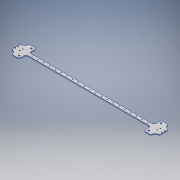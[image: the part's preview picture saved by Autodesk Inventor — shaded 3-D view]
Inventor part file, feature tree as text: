
AUTODESK INVENTOR PART (.ipt)
format: ipt  version: 2017.3 (Build 213256000, 256)  size: 239,104 bytes
history: native  units: mm
features: sketch x5, mirror x3, fillet x3, other x3, extrude x2, sheet_metal_op x1, pattern_linear x1
ambient origin geometry x8: Origin, YZ Plane, XZ Plane, XY Plane, X Axis, Y Axis, Z Axis, Center Point
bodies: Solid1 (feature_tree)
feature tree (18):
  sheet_metal_op  "Face1"
  extrude  "Extrusion1"  Depth=11.0mm
  extrude  "Extrusion2"  Depth=40.0mm
  mirror  "Mirror2"
  pattern_linear  "Rectangular Pattern1"  Count1=3  [1 undecoded]
  mirror  "Mirror3"
  fillet  "Fillet5"  Radius=10.0mm
  fillet  "Fillet6"  Radius=2.5mm
  fillet  "Fillet7"  Radius=15.0mm
  mirror  "Mirror4"
  sketch  "Sketch1"  dims[d0=11.0mm d1=215.0mm]
  other  "Plate1"
  sketch  "Sketch2"  dims[d2=60.0mm d3=40.0mm]
  sketch  "Sketch3"  dims[d4=3.0mm d5=30.0mm d6=10.0mm d7=0.0mm d10=2.5mm d11=15.0mm]
  sketch  "Sketch4"  dims[d12=10.0mm]
  sketch  "Sketch5"  dims[d13=3.0mm d14=10.0mm d15=0.0mm d18=2.5mm d19=3.0mm d20=0.0mm d21=210.0mm d23=20.0mm d24=9.0mm d25=9.0mm d26=5.0mm d27=3.0mm d28=0.0mm d29=6.0mm d30=8.0mm d31=5.5mm]
  other  "Cut1"
  other  "Cut2"
note: 1 required parameter value undecoded (feature->parameter linkage not recoverable at this tier; creation-order binding heuristic only, values carry confidence <= 0.55)
